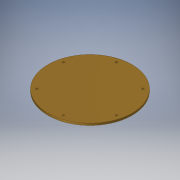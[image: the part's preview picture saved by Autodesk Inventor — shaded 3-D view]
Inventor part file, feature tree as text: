
AUTODESK INVENTOR PART (.ipt)
format: ipt  version: 2018 (Build 220112000, 112)  size: 108,032 bytes
history: native  units: in
note: dims shown in document units (in); Inventor stores cm internally (conversion verified against a paired STEP export)
features: sketch x2, extrude x1, hole x1, pattern_circular x1
ambient origin geometry x8: Origin, YZ Plane, XZ Plane, XY Plane, X Axis, Y Axis, Z Axis, Center Point
bodies: Solid1 (feature_tree)
feature tree (5):
  extrude  "Extrusion1"  Depth=0.1in TaperAngle=0.0deg
  hole  "Hole1"  [1 undecoded]
  pattern_circular  "Circular Pattern1"  Count=6 Angle=360.0deg
  sketch  "Sketch1"  dims[d0=4.2in d1=0.1in d2=0.0in]
  sketch  "Sketch2"  dims[d3=1.875in d4=45.0deg d5=0.094in d6=0.75in d7=0.173in d8=0.25in d9=90.0deg d10=1.0in d11=0.8108in d12=2.3622in d13=360.0deg]
note: 1 required parameter value undecoded (feature->parameter linkage not recoverable at this tier; creation-order binding heuristic only, values carry confidence <= 0.55)
